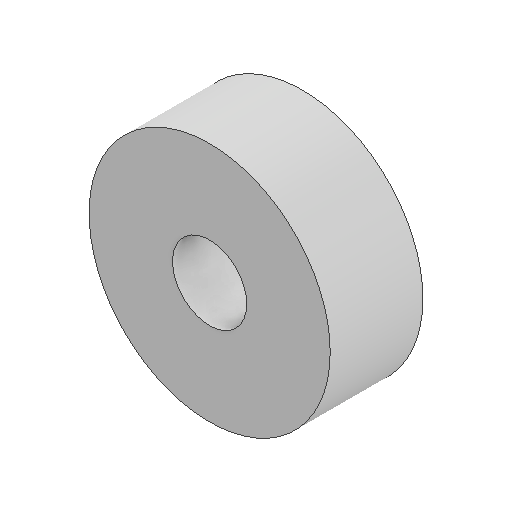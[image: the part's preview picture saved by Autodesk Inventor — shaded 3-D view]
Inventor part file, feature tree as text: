
AUTODESK INVENTOR PART (.ipt)
format: ipt  version: 2022.5 (Build 265521000, 521)  size: 96,256 bytes
history: native  units: mm
features: extrude x1, sketch x1
ambient origin geometry x8: Origin, YZ Plane, XZ Plane, XY Plane, X Axis, Y Axis, Z Axis, Center Point
bodies: Volumenkörper1 (feature_tree)
feature tree (2):
  extrude  "Extrusion1"  Depth=5.0mm
  sketch  "Skizze1"  dims[d0=4.0mm d1=13.0mm d2=5.0mm d3=0.0mm]
